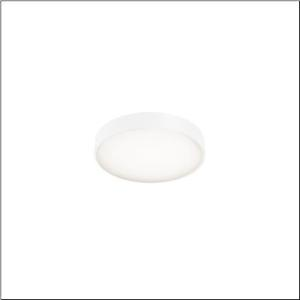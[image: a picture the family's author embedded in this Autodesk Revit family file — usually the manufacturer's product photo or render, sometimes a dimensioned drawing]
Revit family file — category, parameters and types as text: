
# Revit family: round_21_s_51mr34gd0421w
name_source: partatom
category: Lighting Fixtures
units: mm (PartAtom-declared; Revit-internal decimal feet)

## family parameters
Cut with Voids When Loaded = No
Host = Face
Light Source = No
Part Type = Normal
Room Calculation Point = No
Round Connector Dimension = Use Diameter
Shared = No

## types (1)
- Round 21 S (1 x LED, 4090 lm, 28.3 W, 4000K)
    Apparent Load = 28 VA
    CIE Flux Codes = 49 80 96 79 100
    Color Rendering = 80
    Color Temperature = 4000K
    Default Elevation = 1800 mm
    Description = Round 21 S, wall and ceiling luminaire, primary optical cover: cover, of PMMA, opal, light emission: direct/indirect distribution, primary light characteristic: symmetric, installation type: suspended mounting, surface-mounted, LED, rated luminous flux: 4.090lm, luminous efficacy: 135lm/W, light colour: 840, colour temperature: 4000K, control gear: DALI 2, with terminal, 5-pole, mains connection: 230V, AC, 50/60Hz, rated input power: 28.3W, housing, of aluminium, coated, white, diameter: 400mm, height: 62mm, protection rating (complete): IP40, insulation class (complete): insulation class I (protective earthing), certification: CE, impact resistance: IK04, permissible operating ambient temperature: -10..+35°C, packaging unit: 1 piece
    Height = 87 mm
    Lamp = 1 x LED
    Lamp Light Flux = 4090 lm
    Lamp Power = 28.3 W
    Lamp count = 1
    Length = 400 mm
    Luminous efficacy = 145 lm/W
    Manufacturer = Siteco
    ModVariant = No
    Model = 51MR34GD0421W
    Mounting Place = Ceiling
    Mounting Type = Surface mounted
    Number of Poles = 1
    OnlyDefault = Yes
    Power Factor = 1
    Product Name = Round 21 S
    Product group = wall and ceiling luminaire | ceiling mounted
    ProductGroupID = 304
    Protection Class = Protection class I
    Protection Degree = IP 40
    RLX_Detail_Level = 1
    RLX_Emergency_Light_Flux = 0 lm
    RLX_Emergency_Type = 0
    RLX_Emergency_Type_DB = No
    RlxData = <blob elided: 9945 chars, md5=2e0a7899>
    Socket = socket
    Standby Power = 0 W
    System Light Flux = 4090 lm
    System Power = 28 W
    Type Comments = Product without accessories
    Type Image = l_1258307.jpg
    URL = http://relux.com
    VarID = ---
    Voltage = 0 V
    Weight = 0.00 kg
    Width = 0 mm  [stored 0 ft]

note: [stored X ft] marks values corroborated as IEEE doubles in the binary element streams (Revit-internal decimal feet)

## geometry (parser evidence)
native form markers: Sweep x13
no freeform markers — native parametric forms only
